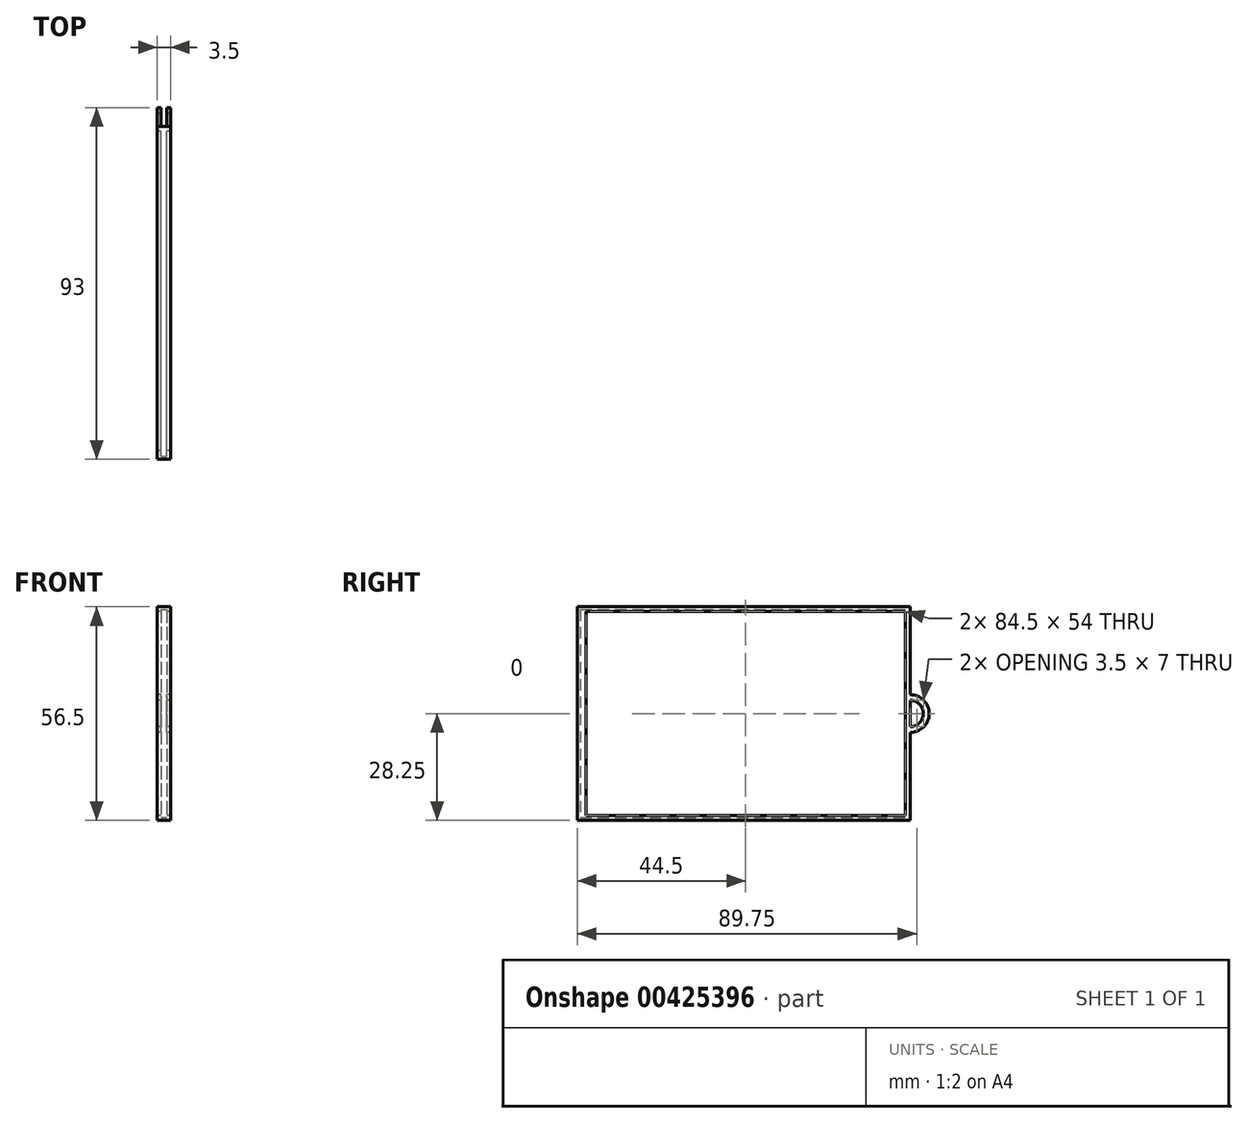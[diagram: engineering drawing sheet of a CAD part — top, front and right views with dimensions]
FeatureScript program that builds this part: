
annotation { "Feature Type Name" : "Feature", "Feature Type Description" : "" }
export const myFeature = defineFeature(function(context is Context, id is Id, definition is map)
    precondition{}
    {
        {
            var Q0;
            Q0=qCreatedBy(makeId("Right.planeOp"),FACE);
            var sketch = newSketch(context, id + "F0", { "sketchPlane" : qUnion([Q0])});
            skLineSegment(sketch, "E0.bottom", {"start": v(-42.75, 27) * mm, "end": v(42.75, 27) * mm});
            skLineSegment(sketch, "E0.top", {"start": v(-42.75, -27) * mm, "end": v(42.75, -27) * mm});
            skLineSegment(sketch, "E0.left", {"start": v(-42.75, 27) * mm, "end": v(-42.75, -27) * mm});
            skLineSegment(sketch, "E0.right", {"start": v(42.75, 27) * mm, "end": v(42.75, -27) * mm});
            skPoint(sketch, "E0.middle", {"position": v(0, 0) * mm});
            skLineSegment(sketch, "E1.bottom", {"start": v(-44, 28.25) * mm, "end": v(44, 28.25) * mm});
            skLineSegment(sketch, "E1.top", {"start": v(-44, -28.25) * mm, "end": v(44, -28.25) * mm});
            skLineSegment(sketch, "E1.left", {"start": v(-44, 28.25) * mm, "end": v(-44, -28.25) * mm});
            skLineSegment(sketch, "E1.right", {"start": v(44, 28.25) * mm, "end": v(44, -28.25) * mm});
            skLineSegment(sketch, "E2.bottom", {"start": v(-41.75, 26) * mm, "end": v(41.75, 26) * mm});
            skLineSegment(sketch, "E2.top", {"start": v(-41.75, -26) * mm, "end": v(41.75, -26) * mm});
            skLineSegment(sketch, "E2.left", {"start": v(-41.75, 26) * mm, "end": v(-41.75, -26) * mm});
            skLineSegment(sketch, "E2.right", {"start": v(41.75, 26) * mm, "end": v(41.75, -26) * mm});
            skPoint(sketch, "E3", {"position": v(-44, 0) * mm});
            skArc(sketch, "E4", {"start": v(44, 5) * mm, "mid": v(49, 0) * mm, "end": v(44, -5) * mm});
            skPoint(sketch, "E5", {"position": v(49, 0) * mm});
            skArc(sketch, "E6", {"start": v(44, 3.5) * mm, "mid": v(47.5, 0) * mm, "end": v(44, -3.5) * mm});
            skPoint(sketch, "E7", {"position": v(-41.75, 28.25) * mm});
            skPoint(sketch, "E8", {"position": v(-41.75, -28.25) * mm});
            skLineSegment(sketch, "E9", {"start": v(-41.75, 28.25) * mm, "end": v(-41.75, -28.25) * mm});
            skSolve(sketch);
        }
        {
            var Q0;
            Q0 = qSketchRegion(id + "F0", true);
            var Q1;
            Q1=makeQuery(id+"F0.imprint","IMPRINT",FACE,{"disambiguationData":[TD([[makeQuery(id+"F0.imprint","IMPRINT",EDGE,{"derivedFrom":sQuery(id+"F0.wireOp",EDGE,"E0.bottom")}),-1.0]])]});
            extrude(context, id + "F1", {"entities" : qUnion([Q0, Q1]), "endBound" : BoundingType.SYMMETRIC, "depth" : 3.5 * mm});
        }
        {
            var Q0;
            Q0=qCreatedBy(makeId("Front.planeOp"),FACE);
            var sketch = newSketch(context, id + "F2", { "sketchPlane" : qUnion([Q0])});
            skLineSegment(sketch, "E10.bottom", {"start": v(-0.75, 27.5) * mm, "end": v(0.75, 27.5) * mm});
            skLineSegment(sketch, "E10.top", {"start": v(-0.75, -27.5) * mm, "end": v(0.75, -27.5) * mm});
            skLineSegment(sketch, "E10.left", {"start": v(-0.75, 27.5) * mm, "end": v(-0.75, -27.5) * mm});
            skLineSegment(sketch, "E10.right", {"start": v(0.75, 27.5) * mm, "end": v(0.75, -27.5) * mm});
            skPoint(sketch, "E10.middle", {"position": v(0, 0) * mm});
            skSolve(sketch);
        }
        {
            var Q0;
            Q0 = qSketchRegion(id + "F2", true);
            extrude(context, id + "F3", {"entities" : qUnion([Q0]), "operationType" : NewBodyOperationType.REMOVE, "depth" : 43.25 * mm, "hasSecondDirection" : true, "secondDirectionOppositeDirection" : true, "secondDirectionDepth" : 58.6 * mm});
        }
    });
